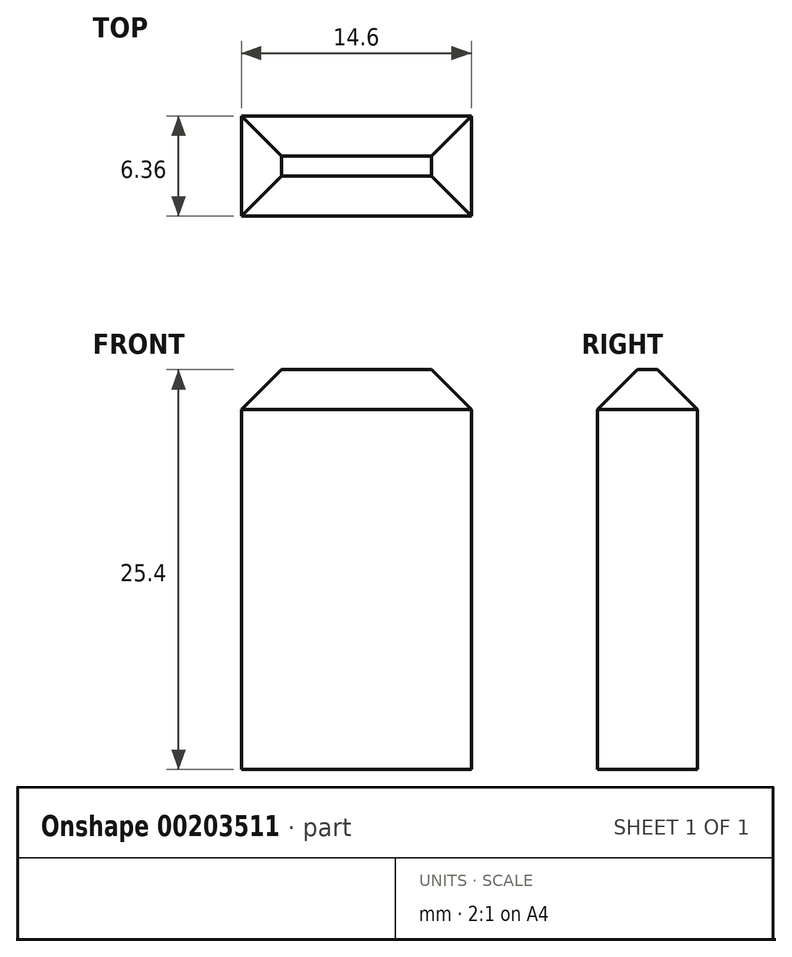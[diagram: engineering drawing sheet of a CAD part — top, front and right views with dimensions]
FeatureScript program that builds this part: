
annotation { "Feature Type Name" : "Feature", "Feature Type Description" : "" }
export const myFeature = defineFeature(function(context is Context, id is Id, definition is map)
    precondition{}
    {
        {
            var Q0;
            Q0=qCreatedBy(makeId("Top.planeOp"),FACE);
            var sketch = newSketch(context, id + "F0", { "sketchPlane" : qUnion([Q0])});
            skLineSegment(sketch, "E0.bottom", {"start": v(7.3, 3.18) * mm, "end": v(-7.3, 3.18) * mm});
            skLineSegment(sketch, "E0.top", {"start": v(7.3, -3.18) * mm, "end": v(-7.3, -3.18) * mm});
            skLineSegment(sketch, "E0.left", {"start": v(7.3, 3.18) * mm, "end": v(7.3, -3.18) * mm});
            skLineSegment(sketch, "E0.right", {"start": v(-7.3, 3.18) * mm, "end": v(-7.3, -3.18) * mm});
            skPoint(sketch, "E0.middle", {"position": v(0, 0) * mm});
            skSolve(sketch);
        }
        {
            var Q0;
            Q0=makeQuery(id+"F0.imprint","IMPRINT",FACE,{"disambiguationData":[TD([[makeQuery(id+"F0.imprint","IMPRINT",EDGE,{"derivedFrom":sQuery(id+"F0.wireOp",EDGE,"E0.bottom")}),1.0]])]});
            extrude(context, id + "F1", {"entities" : qUnion([Q0]), "depth" : 25.4 * mm});
        }
        {
            var Q0;
            Q0=makeQuery(id+"F1.opExtrude","CAP_EDGE",EDGE,{"disambiguationData":[OSD([sQuery(id+"F0.wireOp",EDGE,"E0.top")])],"isStart":false});
            var Q1;
            Q1=makeQuery(id+"F1.opExtrude","CAP_EDGE",EDGE,{"disambiguationData":[OSD([sQuery(id+"F0.wireOp",EDGE,"E0.bottom")])],"isStart":false});
            var Q2;
            Q2=makeQuery(id+"F1.opExtrude","CAP_EDGE",EDGE,{"disambiguationData":[OSD([sQuery(id+"F0.wireOp",EDGE,"E0.right")])],"isStart":false});
            var Q3;
            Q3=makeQuery(id+"F1.opExtrude","CAP_EDGE",EDGE,{"disambiguationData":[OSD([sQuery(id+"F0.wireOp",EDGE,"E0.left")])],"isStart":false});
            chamfer(context, id + "F2", {"entities" : qUnion([Q0, Q1, Q2, Q3]), "width" : 2.54 * mm, "tangentPropagation" : true});
        }
    });
